# Revit family: PROOX Eletronic handdryer EN
name_source: partatom
category: Furniture
revit_build: Autodesk Revit 2014 (Build: 20130308_1515(x64)
units: mm (PartAtom-declared; Revit-internal decimal feet)

## types (2) — shared parameters
BIM objects producer = www.BIMtelligent.eu
Manufacturer = PROOX Ltd.
Product data sheet = http://www.proox.com
URL = http://www.proox.com

## per-type parameters (varying)
| type | Cost | Description | EAN-No. | Material | Model | Specification |
| ONE pure | 569 $ | handdryer PROOX ONE pure made from stainless steel | 9120050350014 | Stainless steel, brushed | PU-010 | Powerful hand dryer made out of stainless steel. Surface with fine brushed structure. Cover 1.5 mm thickness. Intended for wall mounting, with optoelectronic sensor. Perforated design area with 4mm drillings. Drying time less then 10 seconds. Air temperature 55°C, 500W motor, 500W heater element, air output adjustable from 5 to 33cm. Air output adjustable. Automatic switch-off mode after 60 sec. Includes stainless steel screws and anchors. Cables for installation not included. |
| ONE dark passion | 599 $ | handdryer PROOX ONE dark passion made from aluminum black anodized | 9120050350151 | Aluminum, black anodised | DP-010 | Powerful hand dryer made out from glass pearl blasted and black anodised aluminum. Cover 3 mm thickness. Intended for wall mounting, with optoelectronic sensor. Perforated design area with 4mm drillings. Drying time less then 10 seconds. Air temperature 55°C, 500W motor, 500W heater element, Air output adjustable as well as the sensor detection range from 5 to 33cm. Automatic switch-off mode after 60 sec. Includes stainless steel screws and anchors. Cables for installation not included. |

note: column(s) folded — value = type name in every type: Type Comments

## geometry (parser evidence)
native form markers: Sweep x1
no freeform markers — native parametric forms only
